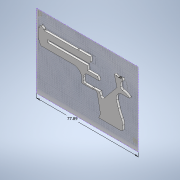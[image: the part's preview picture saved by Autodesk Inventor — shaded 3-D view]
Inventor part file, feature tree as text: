
AUTODESK INVENTOR PART (.ipt)
format: ipt  version: 2022 (Build 260153000, 153)  size: 1,790,976 bytes
history: native  units: in
note: dims shown in document units (in); Inventor stores cm internally (conversion verified against a paired STEP export)
features: other x8, reference x5, sketch x4, sheet_metal_op x3
ambient origin geometry x8: Origin, YZ Plane, XZ Plane, XY Plane, X Axis, Y Axis, Z Axis, Center Point
bodies: Solid1 (feature_tree)
feature tree (20):
  sketch  "Sketch1"  dims[d5=3.0666in]
  sheet_metal_op  "Face1"
  sheet_metal_op  "Face2"
  other  "Image1"
  sketch  "Sketch2"  dims[d16=0.0591in]
  reference  "Reference6"
  other  "Plate1"
  sketch  "Sketch3"  dims[d18=0.0591in]
  other  "Plate2"
  sheet_metal_op  "Bend1"
  sketch  "Sketch4"  dims[d19=0.0591in d20=0.0295in d21=0.1181in d22=0.0591in d23=0.0591in d24=0.0in]
  reference  "Reference8"
  reference  "Reference9"
  reference  "Reference10"
  reference  "Reference11"
  other  "Cut1"
  parser-record x1  (decoder bookkeeping rows leaked as tree rows — omitted from the tree; the rows remain in map.json)
  other  "Assembly1.iam"
  other  "sheetmettaal_2:1"
  other  "sheetmettaal:2"
note: 1 file-system path scrubbed to <path> (originals preserved in map.json)
